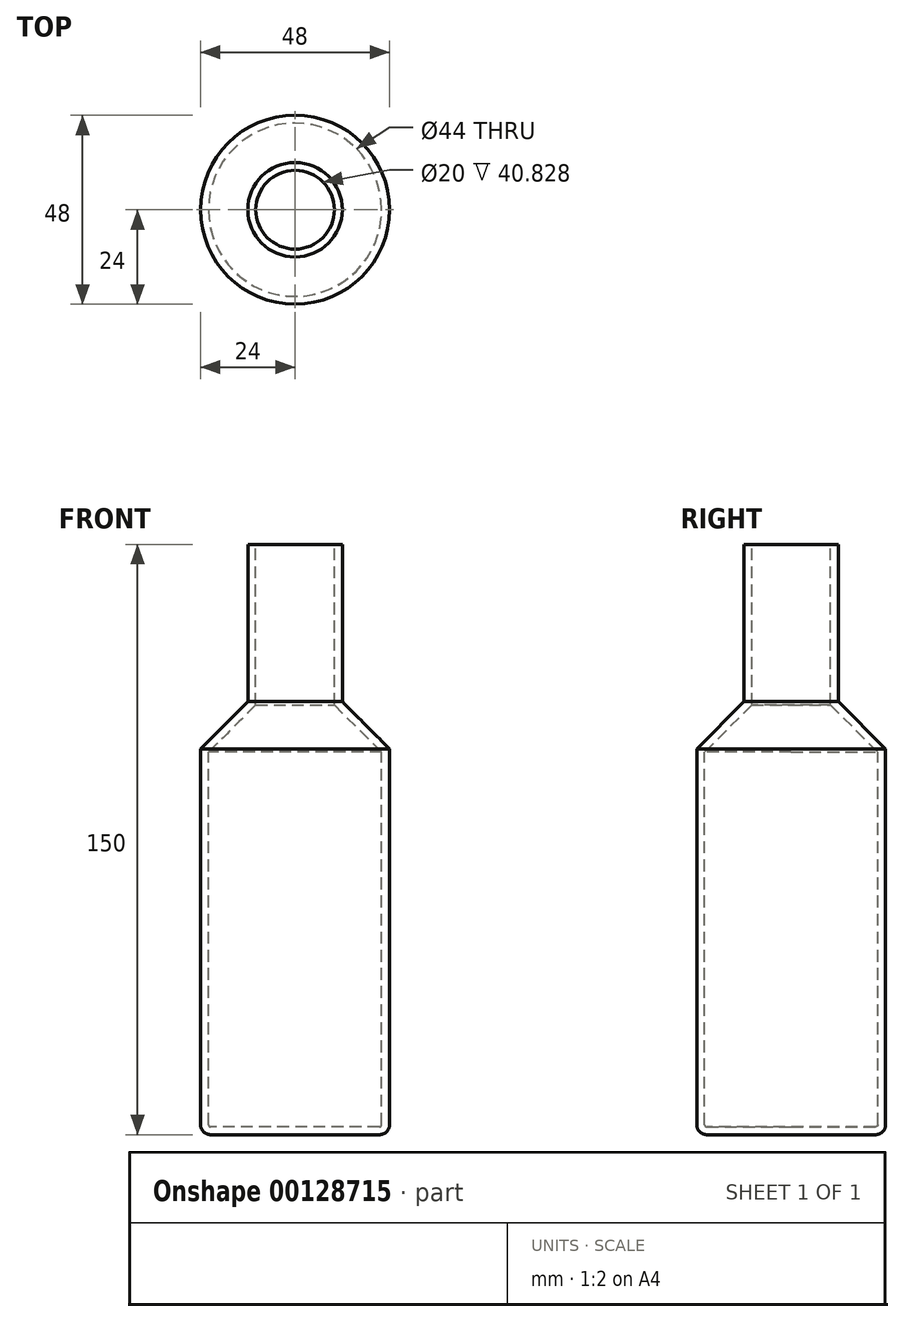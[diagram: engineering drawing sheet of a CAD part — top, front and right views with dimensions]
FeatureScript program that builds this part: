
annotation { "Feature Type Name" : "Feature", "Feature Type Description" : "" }
export const myFeature = defineFeature(function(context is Context, id is Id, definition is map)
    precondition{}
    {
        {
            var Q0;
            Q0=qCreatedBy(makeId("Front.planeOp"),FACE);
            var sketch = newSketch(context, id + "F0", { "sketchPlane" : qUnion([Q0])});
            skLineSegment(sketch, "E0", {"start": v(0, 0.7) * mm, "end": v(24, 0.7) * mm});
            skLineSegment(sketch, "E1", {"start": v(24, 0.7) * mm, "end": v(24, 98.7) * mm});
            skLineSegment(sketch, "E2", {"start": v(24, 98.7) * mm, "end": v(12, 110.7) * mm});
            skLineSegment(sketch, "E3", {"start": v(12, 110.7) * mm, "end": v(12, 150.7) * mm});
            skLineSegment(sketch, "E4", {"start": v(12, 150.7) * mm, "end": v(0, 150.7) * mm});
            skLineSegment(sketch, "E5", {"start": v(0, 150.7) * mm, "end": v(0, 0.7) * mm});
            skSolve(sketch);
        }
        {
            var Q0;
            Q0=makeQuery(id+"F0.imprint","IMPRINT",FACE,{"disambiguationData":[TD([[makeQuery(id+"F0.imprint","IMPRINT",EDGE,{"derivedFrom":sQuery(id+"F0.wireOp",EDGE,"E0")}),1.0]])]});
            var Q1;
            Q1=sQuery(id+"F0.wireOp",EDGE,"E5");
            revolve(context, id + "F1", {"entities" : qUnion([Q0]), "axis" : qUnion([Q1]), "revolveType" : RevolveType.FULL});
        }
        {
            var Q0;
            Q0=makeQuery(id+"F1.opRevolve","SWEPT_EDGE",EDGE,{"disambiguationData":[OSD([sQuery(id+"F0.wireOp",EDGE,"E0"),sQuery(id+"F0.wireOp",EDGE,"E1")])]});
            fillet(context, id + "F2", {"entities" : qUnion([Q0]), "radius" : 2.54 * mm, "tangentPropagation" : true, "allowEdgeOverflow" : false});
        }
        {
            var Q0;
            Q0=makeQuery(id+"F1.opRevolve","SWEPT_FACE",FACE,{"disambiguationData":[OSD([sQuery(id+"F0.wireOp",EDGE,"E4")])]});
            shell(context, id + "F3", {"entities" : qUnion([Q0]), "thickness" : 2 * mm});
        }
    });
